annotation { "Feature Type Name" : "Feature", "Feature Type Description" : "" }
export const myFeature = defineFeature(function(context is Context, id is Id, definition is map)
    precondition{}
    {
        {
            var Q0;
            Q0=qCreatedBy(makeId("Top.planeOp"),FACE);
            var sketch = newSketch(context, id + "F0", { "sketchPlane" : qUnion([Q0])});
            skText(sketch, "E0", { "text": "Kana Matsuda", "fontName": "OpenSans-Regular.ttf"});
            const initialGuessF0  = {"E0": [-0.0512, 0, 1, 0, 0.02685]};
            skSetInitialGuess(sketch, initialGuessF0);
            skSolve(sketch);
        }
        {
            var Q0;
            Q0=qCreatedBy(makeId("Top.planeOp"),FACE);
            var sketch = newSketch(context, id + "F1", { "sketchPlane" : qUnion([Q0])});
            skLineSegment(sketch, "E1.bottom", {"start": v(-48.84, 31.97) * mm, "end": v(195.47, 31.97) * mm});
            skLineSegment(sketch, "E1.top", {"start": v(-48.84, -5.12) * mm, "end": v(195.47, -5.12) * mm});
            skLineSegment(sketch, "E1.left", {"start": v(-55.19, 25.62) * mm, "end": v(-55.19, 1.23) * mm});
            skLineSegment(sketch, "E1.right", {"start": v(201.82, 25.62) * mm, "end": v(201.82, 1.23) * mm});
            skPoint(sketch, "E2.visualSharp", {"position": v(-55.19, 31.97) * mm});
            skArc(sketch, "E2.filletArc", {"start": v(-48.84, 31.97) * mm, "mid": v(-53.33, 30.11) * mm, "end": v(-55.19, 25.62) * mm});
            skPoint(sketch, "E3.visualSharp", {"position": v(201.82, 31.97) * mm});
            skArc(sketch, "E3.filletArc", {"start": v(201.82, 25.62) * mm, "mid": v(199.96, 30.11) * mm, "end": v(195.47, 31.97) * mm});
            skPoint(sketch, "E4.visualSharp", {"position": v(201.82, -5.12) * mm});
            skArc(sketch, "E4.filletArc", {"start": v(195.47, -5.12) * mm, "mid": v(199.96, -3.26) * mm, "end": v(201.82, 1.23) * mm});
            skPoint(sketch, "E5.visualSharp", {"position": v(-55.19, -5.12) * mm});
            skArc(sketch, "E5.filletArc", {"start": v(-55.19, 1.23) * mm, "mid": v(-53.33, -3.26) * mm, "end": v(-48.84, -5.12) * mm});
            skSolve(sketch);
        }
        {
            var Q0;
            Q0 = qSketchRegion(id + "F1", true);
            extrude(context, id + "F2", {"entities" : qUnion([Q0]), "oppositeDirection" : true, "depth" : 25.4 * mm, "offsetDistance" : 25.4 * mm});
        }
        {
            var Q0;
            Q0 = qSketchRegion(id + "F0", true);
            extrude(context, id + "F3", {"entities" : qUnion([Q0]), "operationType" : NewBodyOperationType.REMOVE, "oppositeDirection" : true, "depth" : 19.05 * mm, "offsetDistance" : 25.4 * mm});
        }
    });